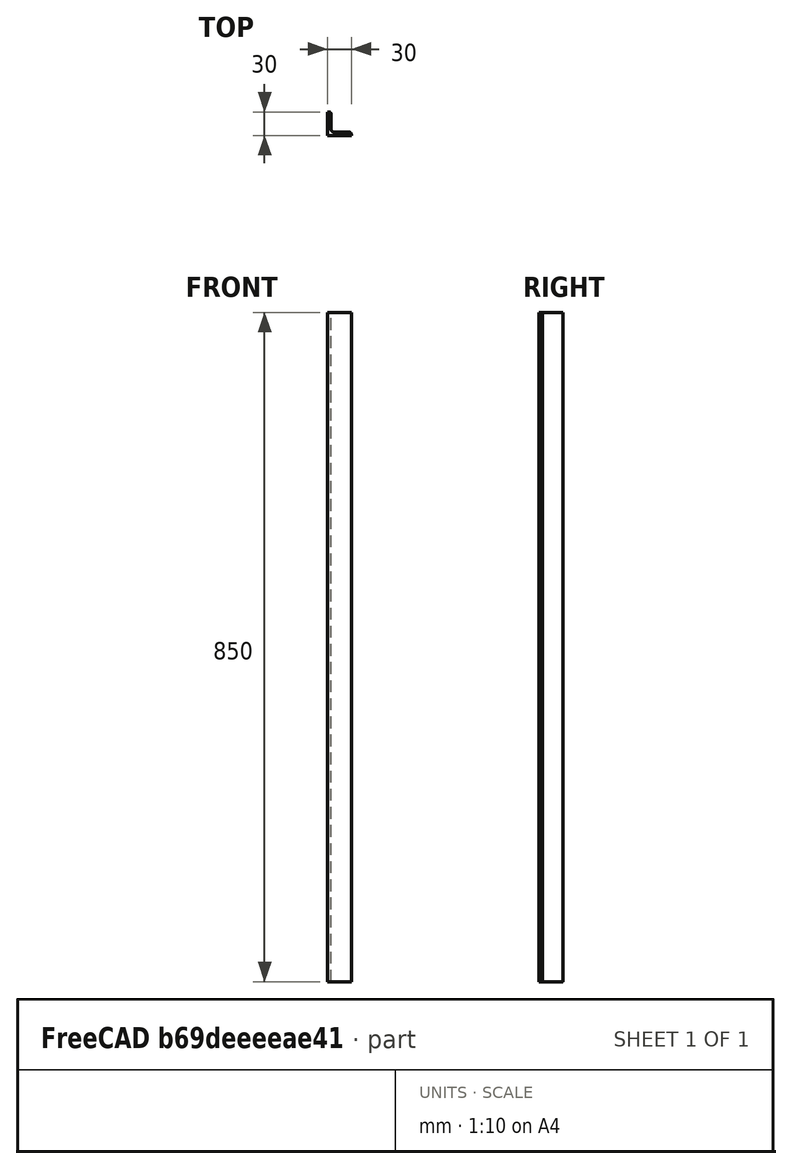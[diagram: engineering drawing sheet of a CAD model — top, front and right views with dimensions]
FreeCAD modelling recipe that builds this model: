
FCSTD DOCUMENT  (FreeCAD 0.21R33771 (Git))
Label: AngolareCarro30x30x4
License: All rights reserved
LicenseURL: http://en.wikipedia.org/wiki/All_rights_reserved
objects: Sketcher::SketchObject×1, PartDesign::Pad×1, PartDesign::Body×1
note: 4 computed .brp shape members not serialized (recipe doc carries the construction recipe); baked Part::Feature solids carry a one-line shape summary decoded from their .brp

FEATURE [Sketcher::SketchObject] Sketch
  FullyConstrained = true
  MapMode = 5
  Support = -> [XY_Plane]
  sketch-geometry (9):
    g0: LineSegment StartX=0 StartY=0 StartZ=0 EndX=30 EndY=0 EndZ=0
    g1: LineSegment StartX=30 StartY=0 StartZ=0 EndX=30 EndY=2 EndZ=0
    g2: LineSegment StartX=28 StartY=4 StartZ=0 EndX=9 EndY=4 EndZ=0
    g3: LineSegment StartX=4 StartY=9 StartZ=0 EndX=4 EndY=28 EndZ=0
    g4: LineSegment StartX=2 StartY=30 StartZ=0 EndX=0 EndY=30 EndZ=0
    g5: LineSegment StartX=0 StartY=30 StartZ=0 EndX=0 EndY=0 EndZ=0
    g6: ArcOfCircle CenterX=9 CenterY=9 CenterZ=0 NormalX=0 NormalY=0 NormalZ=1 AngleXU=0 Radius=5 StartAngle=3.14159 EndAngle=4.71239
    g7: ArcOfCircle CenterX=28 CenterY=2 CenterZ=0 NormalX=0 NormalY=0 NormalZ=1 AngleXU=0 Radius=2 StartAngle=0 EndAngle=1.5708
    g8: ArcOfCircle CenterX=2 CenterY=28 CenterZ=0 NormalX=0 NormalY=0 NormalZ=1 AngleXU=0 Radius=2 StartAngle=0 EndAngle=1.5708
  constraints (23):
    c: PointOnObject(g0,g-1)
    c: Coincident(g1,g0)
    c: Vertical(g1)
    c: Horizontal(g2)
    c: Vertical(g3)
    c: PointOnObject(g4,g-2)
    c: Horizontal(g4)
    c: Coincident(g5,g4)
    c: Coincident(g5,g-1)
    c: Coincident(g0,g5)
    c: DistanceX(g0,g0) = 30
    c: DistanceY(g5,g5) = 30
    c: Tangent(g2,g6) = 1.5708
    c: Tangent(g3,g6) = 1.5708
    c: Tangent(g2,g7) = -1.5708
    c: Tangent(g1,g7) = -1.5708
    c: Tangent(g4,g8) = -1.5708
    c: Tangent(g3,g8) = -1.5708
    c: Radius(g6) = 5
    c: Radius(g8) = 2
    c: Radius(g7) = 2
    c: DistanceY(g0,g2) = 4
    c: DistanceX(g4,g3) = 4
FEATURE [PartDesign::Pad] Pad
  Direction = (0,0,1)
  Length = 850
  Length2 = 10
  Profile = -> Sketch
  ReferenceAxis = -> Sketch [N_Axis]
  Type = 0
FEATURE [PartDesign::Body] Body
  Group = -> [Sketch,Pad]
  Origin = -> Origin
  Tip = -> Pad
